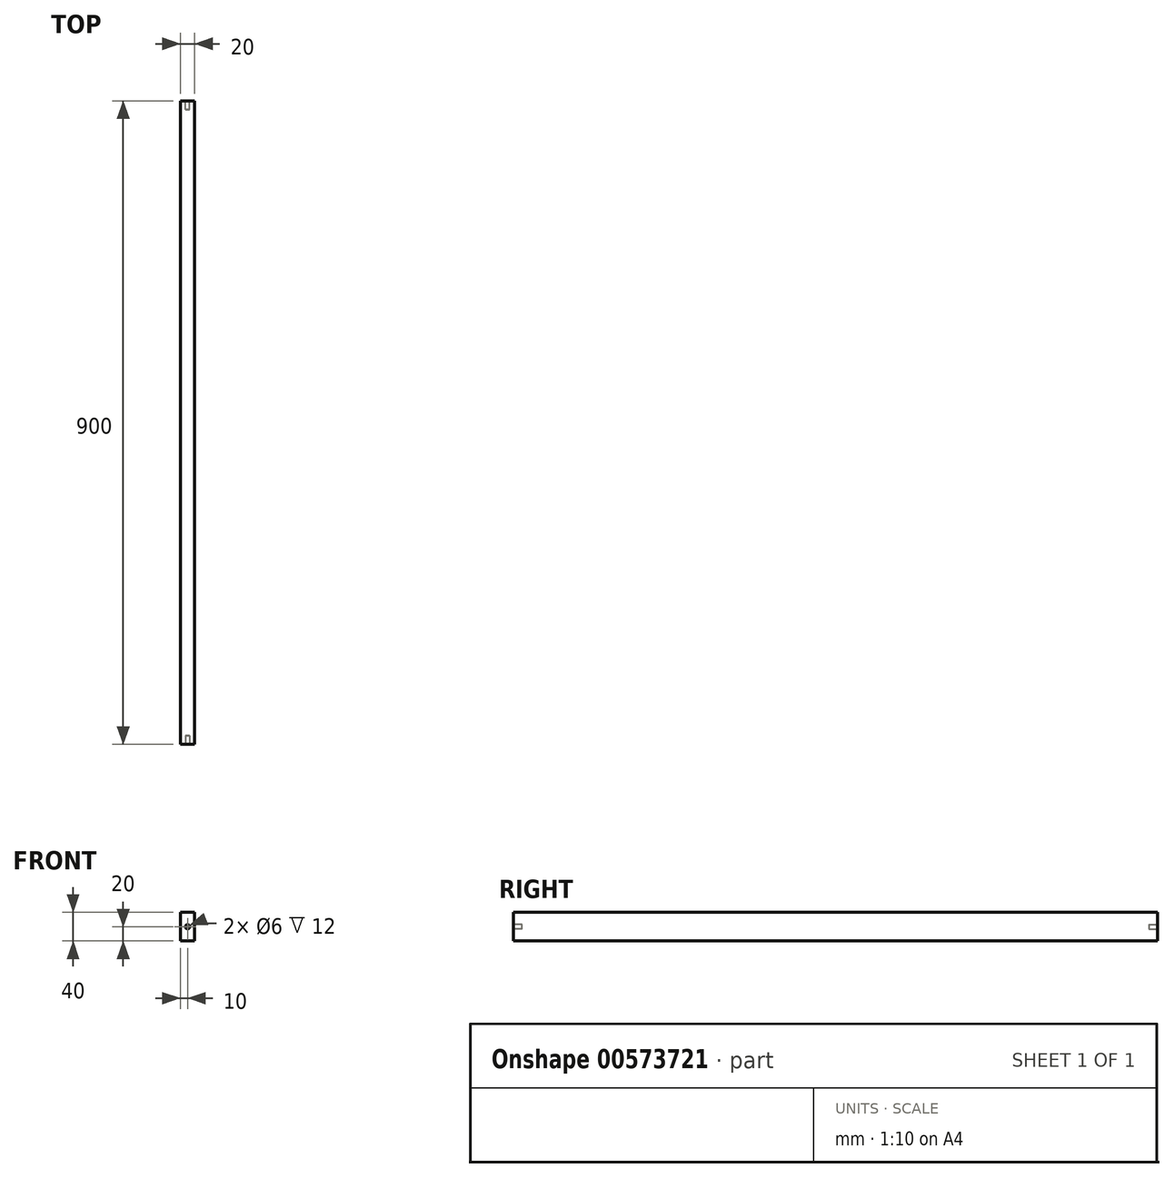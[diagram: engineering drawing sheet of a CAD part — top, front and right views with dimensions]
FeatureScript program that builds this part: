
annotation { "Feature Type Name" : "Feature", "Feature Type Description" : "" }
export const myFeature = defineFeature(function(context is Context, id is Id, definition is map)
    precondition{}
    {
        {
            var Q0;
            Q0=qCreatedBy(makeId("Front.planeOp"),FACE);
            var sketch = newSketch(context, id + "F0", { "sketchPlane" : qUnion([Q0])});
            skLineSegment(sketch, "E0.bottom", {"start": v(0, 0) * mm, "end": v(20, 0) * mm});
            skLineSegment(sketch, "E0.top", {"start": v(0, 40) * mm, "end": v(20, 40) * mm});
            skLineSegment(sketch, "E0.left", {"start": v(0, 0) * mm, "end": v(0, 40) * mm});
            skLineSegment(sketch, "E0.right", {"start": v(20, 0) * mm, "end": v(20, 40) * mm});
            skSolve(sketch);
        }
        {
            var Q0;
            Q0=makeQuery(id+"F0.imprint","IMPRINT",FACE,{"disambiguationData":[TD([[makeQuery(id+"F0.imprint","IMPRINT",EDGE,{"derivedFrom":sQuery(id+"F0.wireOp",EDGE,"E0.bottom")}),1.0]])]});
            extrude(context, id + "F1", {"entities" : qUnion([Q0]), "depth" : 900 * mm, "offsetDistance" : 25 * mm, "symmetric" : true});
        }
        {
            var Q0;
            Q0=makeQuery(id+"F1.opExtrude","CAP_FACE",FACE,{"disambiguationData":[OSD([sQuery(id+"F0.wireOp",EDGE,"E0.bottom"),sQuery(id+"F0.wireOp",EDGE,"E0.top"),sQuery(id+"F0.wireOp",EDGE,"E0.left"),sQuery(id+"F0.wireOp",EDGE,"E0.right")])],"isStart":false});
            var sketch = newSketch(context, id + "F2", { "sketchPlane" : qUnion([Q0])});
            skCircle(sketch, "E1", {"center": v(10, 20) * mm, "radius": 3 * mm});
            skSolve(sketch);
        }
        {
            var Q0;
            Q0=makeQuery(id+"F2.imprint","IMPRINT",FACE,{"disambiguationData":[TD([[makeQuery(id+"F2.imprint","IMPRINT",EDGE,{"derivedFrom":sQuery(id+"F2.wireOp",EDGE,"E1")}),1.0]])]});
            extrude(context, id + "F3", {"entities" : qUnion([Q0]), "operationType" : NewBodyOperationType.REMOVE, "oppositeDirection" : true, "depth" : 12 * mm, "offsetDistance" : 25 * mm});
        }
        {
            var Q0;
            Q0=makeQuery(id+"F1.opExtrude","CAP_FACE",FACE,{"disambiguationData":[OSD([sQuery(id+"F0.wireOp",EDGE,"E0.bottom"),sQuery(id+"F0.wireOp",EDGE,"E0.top"),sQuery(id+"F0.wireOp",EDGE,"E0.left"),sQuery(id+"F0.wireOp",EDGE,"E0.right")])],"isStart":true});
            var sketch = newSketch(context, id + "F4", { "sketchPlane" : qUnion([Q0])});
            skCircle(sketch, "E2", {"center": v(-10, 20) * mm, "radius": 3 * mm});
            skSolve(sketch);
        }
        {
            var Q0;
            Q0=makeQuery(id+"F4.imprint","IMPRINT",FACE,{"disambiguationData":[TD([[makeQuery(id+"F4.imprint","IMPRINT",EDGE,{"derivedFrom":sQuery(id+"F4.wireOp",EDGE,"E2")}),1.0]])]});
            extrude(context, id + "F5", {"entities" : qUnion([Q0]), "operationType" : NewBodyOperationType.REMOVE, "oppositeDirection" : true, "depth" : 12 * mm, "offsetDistance" : 25 * mm});
        }
    });
